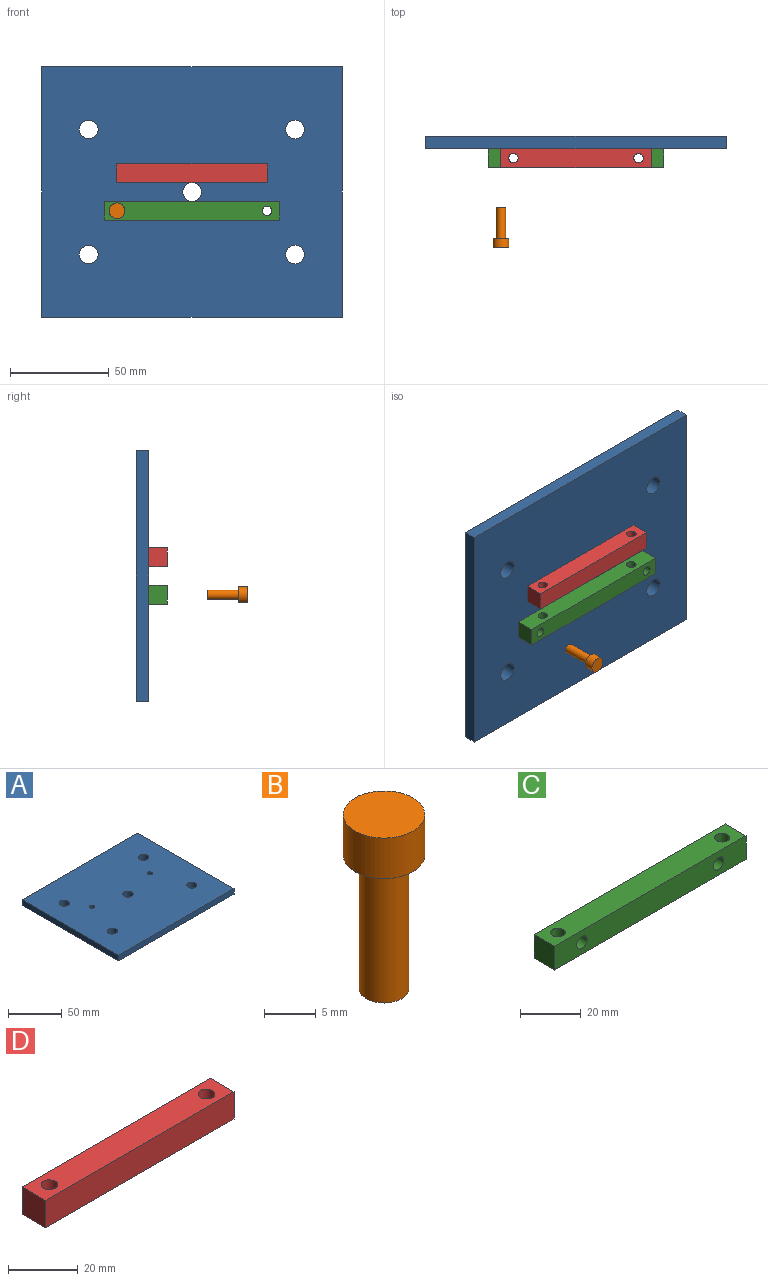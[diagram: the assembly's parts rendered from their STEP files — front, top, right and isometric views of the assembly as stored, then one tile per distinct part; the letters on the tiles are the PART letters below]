
ASSEMBLY  parts=4 mates=5
PART A: 13 faces, bbox 152.4x127x6.4 mm
  f0: plane 127x6.35mm, normal (-1,0,0), area 806.5mm2, adj f1,f9,f11,f12
  f1: plane 152.4x6.35mm, normal (0,-1,0), area 967.7mm2, adj f0,f2,f11,f12
  f2: plane 127x6.35mm, normal (1,0,0), area 806.5mm2, adj f1,f9,f11,f12
  f3: cylinder r=2.41mm len=6.35mm, axis (0,0,-1), area 96.3mm2, adj f11,f12
  f4: cylinder r=4.76mm len=9.53mm, axis (0,0,-1), area 190mm2, adj f11,f12
  f5: cylinder r=4.76mm len=9.53mm, axis (0,0,-1), area 190mm2, adj f11,f12
  f6: cylinder r=4.76mm len=9.53mm, axis (0,0,-1), area 190mm2, adj f11,f12
  f7: cylinder r=4.76mm len=9.53mm, axis (0,0,-1), area 190mm2, adj f11,f12
  f8: cylinder r=4.76mm len=9.53mm, axis (0,0,-1), area 190mm2, adj f11,f12
  f9: plane 152.4x6.35mm, normal (0,1,0), area 967.7mm2, adj f0,f2,f11,f12
  f10: cylinder r=2.41mm len=6.35mm, axis (0,0,-1), area 96.3mm2, adj f11,f12
  f11: plane 152.4x127mm, normal (0,0,1), area 18961.9mm2, adj f0,f1,f2,f3,f4,f5,f6,f7
  f12: plane 152.4x127mm, normal (0,0,-1), area 18961.9mm2, adj f0,f1,f2,f3,f4,f5,f6,f7
PART B: 5 faces, bbox 7.9x7.9x20.7 mm
  f0: plane 7.92x7.92mm, normal (0,0,1), area 49.3mm2, adj f4
  f1: plane 4.83x4.83mm, normal (0,0,-1), area 18.3mm2, adj f2
  f2: cylinder r=2.41mm len=15.88mm, axis (0,0,1), area 240.7mm2, adj f1,f3
  f3: plane 7.92x7.92mm, normal (0,0,-1), area 31mm2, adj f2,f4
  f4: cylinder r=3.96mm len=7.92mm, axis (0,0,1), area 120.2mm2, adj f0,f3
PART C: 10 faces, bbox 88.9x9.5x9.5 mm
  f0: plane 9.53x9.53mm, normal (-1,0,0), area 90.7mm2, adj f1,f4,f6,f7
  f1: plane 88.9x9.53mm, normal (0,-1,0), area 810.2mm2, adj f0,f2,f6,f7,f8,f9
  f2: plane 9.53x9.53mm, normal (1,0,0), area 90.7mm2, adj f1,f4,f6,f7
  f3: cylinder r=2.41mm len=9.53mm, axis (0,0,-1), area 144.4mm2, adj f6,f7
  f4: plane 88.9x9.53mm, normal (0,1,0), area 810.2mm2, adj f0,f2,f6,f7,f8,f9
  f5: cylinder r=2.41mm len=9.53mm, axis (0,0,-1), area 144.4mm2, adj f6,f7
  f6: plane 88.9x9.53mm, normal (0,0,1), area 810.2mm2, adj f0,f1,f2,f3,f4,f5
  f7: plane 88.9x9.53mm, normal (0,0,-1), area 810.2mm2, adj f0,f1,f2,f3,f4,f5
  f8: cylinder r=2.41mm len=9.53mm, axis (0,1,0), area 144.4mm2, adj f1,f4
  f9: cylinder r=2.41mm len=9.53mm, axis (0,1,0), area 144.4mm2, adj f1,f4
PART D: 8 faces, bbox 76.2x9.5x9.5 mm
  f0: plane 9.53x9.53mm, normal (-1,0,0), area 90.7mm2, adj f1,f4,f6,f7
  f1: plane 76.2x9.53mm, normal (0,-1,0), area 725.8mm2, adj f0,f2,f6,f7
  f2: plane 9.53x9.53mm, normal (1,0,0), area 90.7mm2, adj f1,f4,f6,f7
  f3: cylinder r=2.41mm len=9.53mm, axis (0,0,-1), area 144.4mm2, adj f6,f7
  f4: plane 76.2x9.53mm, normal (0,1,0), area 725.8mm2, adj f0,f2,f6,f7
  f5: cylinder r=2.41mm len=9.53mm, axis (0,0,-1), area 144.4mm2, adj f6,f7
  f6: plane 76.2x9.53mm, normal (0,0,1), area 689.2mm2, adj f0,f1,f2,f3,f4,f5
  f7: plane 76.2x9.53mm, normal (0,0,-1), area 689.2mm2, adj f0,f1,f2,f3,f4,f5
PLACE A rot(axis=(-1,0,0),90deg) t=(38.71,2.58,102.14)mm
PLACE B rot(axis=(1,0,0),90deg) t=(76.81,-27.05,29.11)mm
PLACE C rot(axis=(1,0,0),90deg) t=(70.46,2.58,24.35)mm
PLACE D rot(axis=(0,1,0),180deg) t=(153.01,-6.95,52.93)mm
MATE revolute C.f3 <-> A.f10  axis (0,1,0) through (76.81,2.58,29.11)mm
MATE planar D.f4 <-> A.f12  axis (0,1,0) through (114.91,2.58,48.16)mm
MATE revolute D.f5 <-> C.f8  axis (0,0,-1) through (83.16,-2.19,43.4)mm
MATE cylindrical B.f2 <-> C.f3  axis (0,-1,0) through (76.81,-34.98,29.11)mm
MATE parallel C.f0 <-> A.f0  axis (-1,0,0) through (70.46,-2.19,29.11)mm
